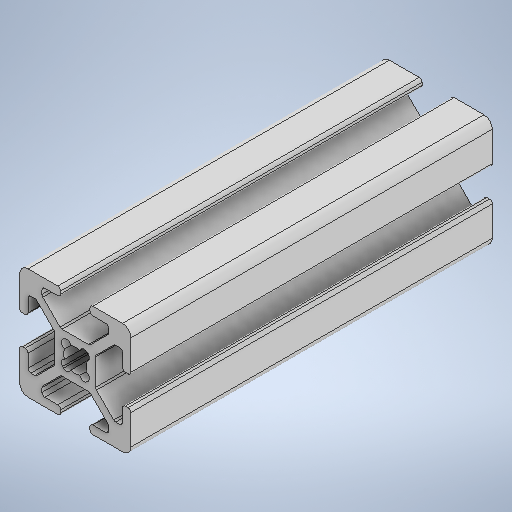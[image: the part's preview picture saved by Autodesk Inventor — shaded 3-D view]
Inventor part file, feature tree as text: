
AUTODESK INVENTOR PART (.ipt)
format: ipt  version: 2025 (Build 290162000, 162)  size: 367,616 bytes
history: native  units: mm
features: extrude x1, sketch x1
ambient origin geometry x8: Origin, YZ Plane, XZ Plane, XY Plane, X Axis, Y Axis, Z Axis, Center Point
bodies: Solid1 (feature_tree)
feature tree (2):
  extrude  "Extrusion1"  Depth=65.0mm
  sketch  "Sketch1"  dims[d0=65.0mm d1=0.0mm d2=1.0mm d3=1.0mm d4=1.0mm d5=0.15mm d6=0.25mm d7=0.375mm d8=14.3117mm d9=0.75mm d10=20.594885mm d11=0.0625mm d12=0.75mm d13=0.375mm]
